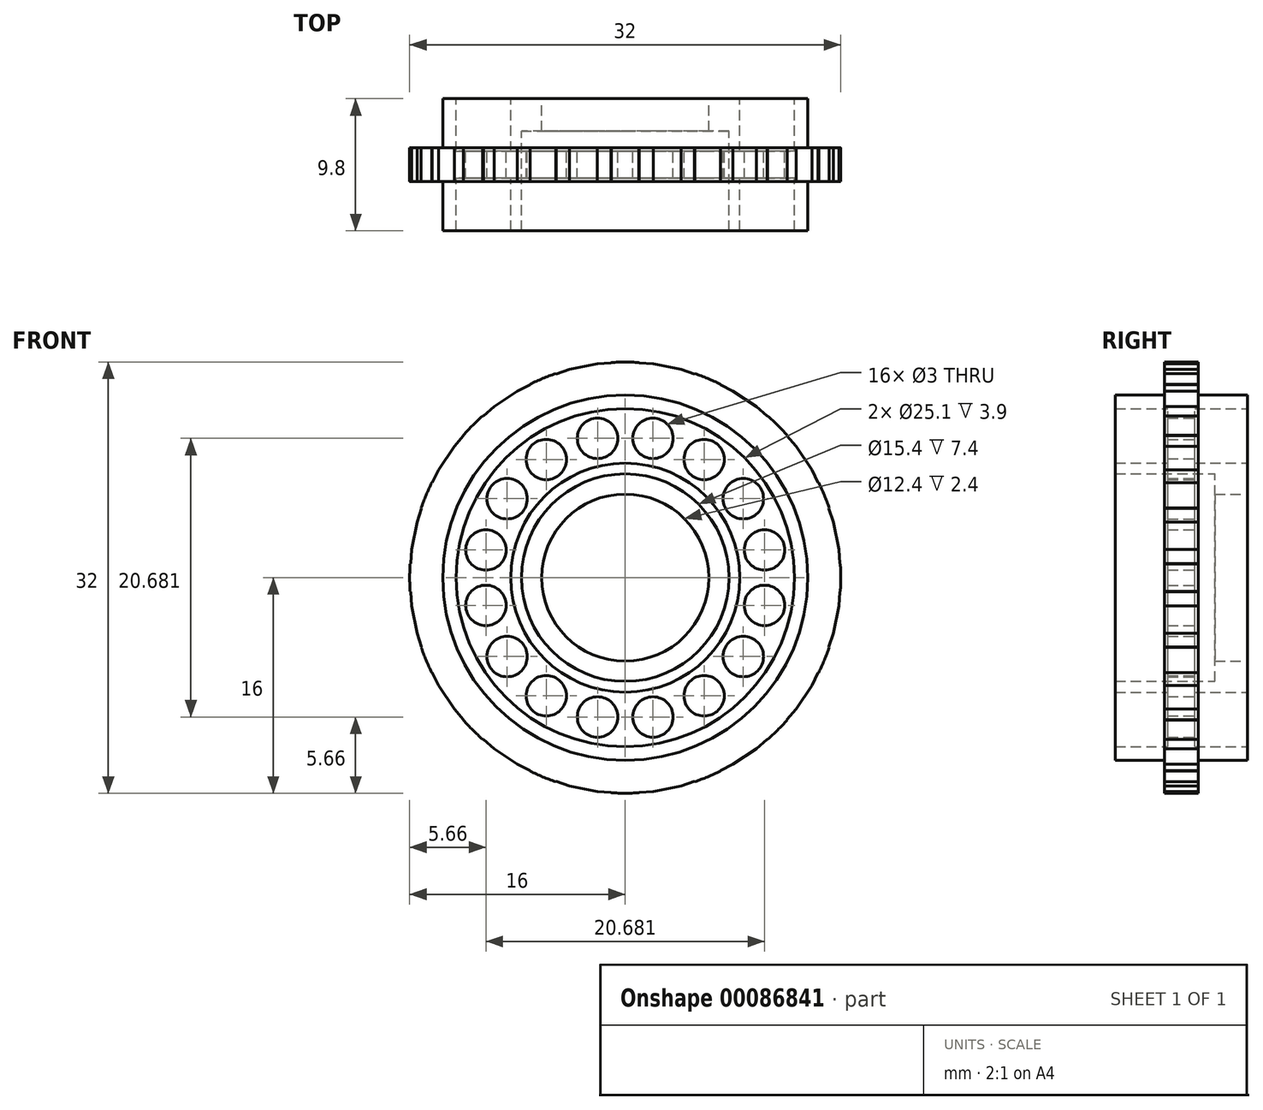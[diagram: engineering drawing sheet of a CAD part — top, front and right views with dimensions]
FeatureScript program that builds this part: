
annotation { "Feature Type Name" : "Feature", "Feature Type Description" : "" }
export const myFeature = defineFeature(function(context is Context, id is Id, definition is map)
    precondition{}
    {
        {
            var Q0;
            Q0=qCreatedBy(makeId("Front.planeOp"),FACE);
            var sketch = newSketch(context, id + "F0", { "sketchPlane" : qUnion([Q0])});
            skCircle(sketch, "E0", {"center": v(0, 0) * mm, "radius": 13.55 * mm});
            skCircle(sketch, "E1", {"center": v(0, 0) * mm, "radius": 12.55 * mm});
            skCircle(sketch, "E2", {"center": v(0, 0) * mm, "radius": 7.7 * mm});
            skCircle(sketch, "E3", {"center": v(0, 0) * mm, "radius": 8.5 * mm});
            skLineSegment(sketch, "E4.1", {"start": v(2.09, 15.86) * mm, "end": v(4.14, 15.45) * mm});
            skLineSegment(sketch, "E4.4", {"start": v(8, 13.86) * mm, "end": v(9.74, 12.7) * mm});
            skLineSegment(sketch, "E4.7", {"start": v(12.7, 9.74) * mm, "end": v(13.86, 8) * mm});
            skLineSegment(sketch, "E4.10", {"start": v(15.45, 4.14) * mm, "end": v(15.86, 2.09) * mm});
            skLineSegment(sketch, "E4.13", {"start": v(15.86, -2.09) * mm, "end": v(15.45, -4.14) * mm});
            skLineSegment(sketch, "E4.16", {"start": v(13.86, -8) * mm, "end": v(12.7, -9.74) * mm});
            skLineSegment(sketch, "E4.19", {"start": v(9.74, -12.7) * mm, "end": v(8, -13.86) * mm});
            skLineSegment(sketch, "E4.22", {"start": v(4.14, -15.45) * mm, "end": v(2.09, -15.86) * mm});
            skLineSegment(sketch, "E4.25", {"start": v(-2.09, -15.86) * mm, "end": v(-4.14, -15.45) * mm});
            skLineSegment(sketch, "E4.28", {"start": v(-8, -13.86) * mm, "end": v(-9.74, -12.7) * mm});
            skLineSegment(sketch, "E4.31", {"start": v(-12.7, -9.74) * mm, "end": v(-13.86, -8) * mm});
            skLineSegment(sketch, "E4.34", {"start": v(-15.45, -4.14) * mm, "end": v(-15.86, -2.09) * mm});
            skLineSegment(sketch, "E4.37", {"start": v(-15.86, 2.09) * mm, "end": v(-15.45, 4.14) * mm});
            skLineSegment(sketch, "E4.40", {"start": v(-13.86, 8) * mm, "end": v(-12.7, 9.74) * mm});
            skLineSegment(sketch, "E4.43", {"start": v(-9.74, 12.7) * mm, "end": v(-8, 13.86) * mm});
            skLineSegment(sketch, "E4.46", {"start": v(-4.14, 15.45) * mm, "end": v(-2.09, 15.86) * mm});
            skLineSegment(sketch, "E5", {"start": v(-1.04, 15.93) * mm, "end": v(0, 17.55) * mm});
            skLineSegment(sketch, "E6", {"start": v(0, 17.55) * mm, "end": v(1.04, 15.93) * mm});
            skLineSegment(sketch, "E7", {"start": v(-6.72, 16.21) * mm, "end": v(-7.06, 14.32) * mm});
            skLineSegment(sketch, "E8", {"start": v(-6.72, 16.21) * mm, "end": v(-5.13, 15.12) * mm});
            skLineSegment(sketch, "E9", {"start": v(6.72, 16.21) * mm, "end": v(5.13, 15.12) * mm});
            skLineSegment(sketch, "E10", {"start": v(6.72, 16.21) * mm, "end": v(7.06, 14.32) * mm});
            skLineSegment(sketch, "E11", {"start": v(10.53, 12) * mm, "end": v(12.4, 12.4) * mm});
            skLineSegment(sketch, "E12", {"start": v(12.4, 12.4) * mm, "end": v(12, 10.53) * mm});
            skLineSegment(sketch, "E13", {"start": v(14.32, 7.06) * mm, "end": v(16.21, 6.72) * mm});
            skLineSegment(sketch, "E14", {"start": v(16.21, 6.72) * mm, "end": v(15.12, 5.13) * mm});
            skLineSegment(sketch, "E15", {"start": v(15.93, 1.04) * mm, "end": v(17.55, 0) * mm});
            skLineSegment(sketch, "E16", {"start": v(17.55, 0) * mm, "end": v(15.93, -1.04) * mm});
            skLineSegment(sketch, "E17", {"start": v(-10.53, 12) * mm, "end": v(-12.4, 12.4) * mm});
            skLineSegment(sketch, "E18", {"start": v(-12, 10.53) * mm, "end": v(-12.4, 12.4) * mm});
            skLineSegment(sketch, "E19", {"start": v(-14.32, 7.06) * mm, "end": v(-16.21, 6.72) * mm});
            skLineSegment(sketch, "E20", {"start": v(-15.12, 5.13) * mm, "end": v(-16.21, 6.72) * mm});
            skLineSegment(sketch, "E21", {"start": v(-15.93, 1.04) * mm, "end": v(-17.55, 0) * mm});
            skLineSegment(sketch, "E22", {"start": v(-15.93, -1.04) * mm, "end": v(-17.55, 0) * mm});
            skLineSegment(sketch, "E23", {"start": v(-15.12, -5.13) * mm, "end": v(-16.21, -6.72) * mm});
            skLineSegment(sketch, "E24", {"start": v(-14.32, -7.06) * mm, "end": v(-16.21, -6.72) * mm});
            skLineSegment(sketch, "E25", {"start": v(-12, -10.53) * mm, "end": v(-12.4, -12.4) * mm});
            skLineSegment(sketch, "E26", {"start": v(-10.53, -12) * mm, "end": v(-12.4, -12.4) * mm});
            skLineSegment(sketch, "E27", {"start": v(-7.06, -14.32) * mm, "end": v(-6.72, -16.21) * mm});
            skLineSegment(sketch, "E28", {"start": v(-5.13, -15.12) * mm, "end": v(-6.72, -16.21) * mm});
            skLineSegment(sketch, "E29", {"start": v(-1.04, -15.93) * mm, "end": v(0, -17.55) * mm});
            skLineSegment(sketch, "E30", {"start": v(1.04, -15.93) * mm, "end": v(0, -17.55) * mm});
            skLineSegment(sketch, "E31", {"start": v(5.13, -15.12) * mm, "end": v(6.72, -16.21) * mm});
            skLineSegment(sketch, "E32", {"start": v(7.06, -14.32) * mm, "end": v(6.72, -16.21) * mm});
            skLineSegment(sketch, "E33", {"start": v(10.53, -12) * mm, "end": v(12.4, -12.4) * mm});
            skLineSegment(sketch, "E34", {"start": v(12, -10.53) * mm, "end": v(12.4, -12.4) * mm});
            skLineSegment(sketch, "E35", {"start": v(14.32, -7.06) * mm, "end": v(16.21, -6.72) * mm});
            skLineSegment(sketch, "E36", {"start": v(15.12, -5.13) * mm, "end": v(16.21, -6.72) * mm});
            skLineSegment(sketch, "E37", {"start": v(0, 12.55) * mm, "end": v(0, 8.5) * mm, "construction": true});
            skCircle(sketch, "E38.cCircle", {"center": v(0, 0) * mm, "radius": 10.34 * mm, "construction": true});
            skLineSegment(sketch, "E38.0", {"start": v(-2.06, 10.34) * mm, "end": v(2.06, 10.34) * mm, "construction": true});
            skLineSegment(sketch, "E38.1", {"start": v(2.06, 10.34) * mm, "end": v(5.86, 8.77) * mm, "construction": true});
            skLineSegment(sketch, "E38.2", {"start": v(5.86, 8.77) * mm, "end": v(8.77, 5.86) * mm, "construction": true});
            skLineSegment(sketch, "E38.3", {"start": v(8.77, 5.86) * mm, "end": v(10.34, 2.06) * mm, "construction": true});
            skLineSegment(sketch, "E38.4", {"start": v(10.34, 2.06) * mm, "end": v(10.34, -2.06) * mm, "construction": true});
            skLineSegment(sketch, "E38.5", {"start": v(10.34, -2.06) * mm, "end": v(8.77, -5.86) * mm, "construction": true});
            skLineSegment(sketch, "E38.6", {"start": v(8.77, -5.86) * mm, "end": v(5.86, -8.77) * mm, "construction": true});
            skLineSegment(sketch, "E38.7", {"start": v(5.86, -8.77) * mm, "end": v(2.06, -10.34) * mm, "construction": true});
            skLineSegment(sketch, "E38.8", {"start": v(2.06, -10.34) * mm, "end": v(-2.06, -10.34) * mm, "construction": true});
            skLineSegment(sketch, "E38.9", {"start": v(-2.06, -10.34) * mm, "end": v(-5.86, -8.77) * mm, "construction": true});
            skLineSegment(sketch, "E38.10", {"start": v(-5.86, -8.77) * mm, "end": v(-8.77, -5.86) * mm, "construction": true});
            skLineSegment(sketch, "E38.11", {"start": v(-8.77, -5.86) * mm, "end": v(-10.34, -2.06) * mm, "construction": true});
            skLineSegment(sketch, "E38.12", {"start": v(-10.34, -2.06) * mm, "end": v(-10.34, 2.06) * mm, "construction": true});
            skLineSegment(sketch, "E38.13", {"start": v(-10.34, 2.06) * mm, "end": v(-8.77, 5.86) * mm, "construction": true});
            skLineSegment(sketch, "E38.14", {"start": v(-8.77, 5.86) * mm, "end": v(-5.86, 8.77) * mm, "construction": true});
            skLineSegment(sketch, "E38.15", {"start": v(-5.86, 8.77) * mm, "end": v(-2.06, 10.34) * mm, "construction": true});
            skCircle(sketch, "E39", {"center": v(-5.86, 8.77) * mm, "radius": 1.5 * mm});
            skCircle(sketch, "E40", {"center": v(-2.06, 10.34) * mm, "radius": 1.5 * mm});
            skCircle(sketch, "E41", {"center": v(2.06, 10.34) * mm, "radius": 1.5 * mm});
            skCircle(sketch, "E42", {"center": v(5.86, 8.77) * mm, "radius": 1.5 * mm});
            skCircle(sketch, "E43", {"center": v(8.77, 5.86) * mm, "radius": 1.5 * mm});
            skCircle(sketch, "E44", {"center": v(10.34, 2.06) * mm, "radius": 1.5 * mm});
            skCircle(sketch, "E45", {"center": v(10.34, -2.06) * mm, "radius": 1.5 * mm});
            skCircle(sketch, "E46", {"center": v(8.77, -5.86) * mm, "radius": 1.5 * mm});
            skCircle(sketch, "E47", {"center": v(5.86, -8.77) * mm, "radius": 1.5 * mm});
            skCircle(sketch, "E48", {"center": v(2.06, -10.34) * mm, "radius": 1.5 * mm});
            skCircle(sketch, "E49", {"center": v(-2.06, -10.34) * mm, "radius": 1.5 * mm});
            skCircle(sketch, "E50", {"center": v(-5.86, -8.77) * mm, "radius": 1.5 * mm});
            skCircle(sketch, "E51", {"center": v(-8.77, -5.86) * mm, "radius": 1.5 * mm});
            skCircle(sketch, "E52", {"center": v(-10.34, -2.06) * mm, "radius": 1.5 * mm});
            skCircle(sketch, "E53", {"center": v(-10.34, 2.06) * mm, "radius": 1.5 * mm});
            skCircle(sketch, "E54", {"center": v(-8.77, 5.86) * mm, "radius": 1.5 * mm});
            skLineSegment(sketch, "E55", {"start": v(-15.45, 4.14) * mm, "end": v(-15.12, 5.13) * mm});
            skLineSegment(sketch, "E56", {"start": v(-14.32, 7.06) * mm, "end": v(-13.86, 8) * mm});
            skLineSegment(sketch, "E57", {"start": v(-12.7, 9.74) * mm, "end": v(-12, 10.53) * mm});
            skLineSegment(sketch, "E58", {"start": v(-10.53, 12) * mm, "end": v(-9.74, 12.7) * mm});
            skLineSegment(sketch, "E59", {"start": v(-8, 13.86) * mm, "end": v(-7.06, 14.32) * mm});
            skLineSegment(sketch, "E60", {"start": v(-5.13, 15.12) * mm, "end": v(-4.14, 15.45) * mm});
            skLineSegment(sketch, "E61", {"start": v(-2.09, 15.86) * mm, "end": v(-1.04, 15.93) * mm});
            skLineSegment(sketch, "E62", {"start": v(1.04, 15.93) * mm, "end": v(2.09, 15.86) * mm});
            skLineSegment(sketch, "E63", {"start": v(4.14, 15.45) * mm, "end": v(5.13, 15.12) * mm});
            skLineSegment(sketch, "E64", {"start": v(7.06, 14.32) * mm, "end": v(8, 13.86) * mm});
            skLineSegment(sketch, "E65", {"start": v(9.74, 12.7) * mm, "end": v(10.53, 12) * mm});
            skLineSegment(sketch, "E66", {"start": v(12, 10.53) * mm, "end": v(12.7, 9.74) * mm});
            skLineSegment(sketch, "E67", {"start": v(13.86, 8) * mm, "end": v(14.32, 7.06) * mm});
            skLineSegment(sketch, "E68", {"start": v(15.12, 5.13) * mm, "end": v(15.45, 4.14) * mm});
            skLineSegment(sketch, "E69", {"start": v(15.86, 2.09) * mm, "end": v(15.93, 1.04) * mm});
            skLineSegment(sketch, "E70", {"start": v(15.93, -1.04) * mm, "end": v(15.86, -2.09) * mm});
            skLineSegment(sketch, "E71", {"start": v(15.45, -4.14) * mm, "end": v(15.12, -5.13) * mm});
            skLineSegment(sketch, "E72", {"start": v(14.32, -7.06) * mm, "end": v(13.86, -8) * mm});
            skLineSegment(sketch, "E73", {"start": v(12.7, -9.74) * mm, "end": v(12, -10.53) * mm});
            skLineSegment(sketch, "E74", {"start": v(10.53, -12) * mm, "end": v(9.74, -12.7) * mm});
            skLineSegment(sketch, "E75", {"start": v(8, -13.86) * mm, "end": v(7.06, -14.32) * mm});
            skLineSegment(sketch, "E76", {"start": v(5.13, -15.12) * mm, "end": v(4.14, -15.45) * mm});
            skLineSegment(sketch, "E77", {"start": v(2.09, -15.86) * mm, "end": v(1.04, -15.93) * mm});
            skLineSegment(sketch, "E78", {"start": v(-1.04, -15.93) * mm, "end": v(-2.09, -15.86) * mm});
            skLineSegment(sketch, "E79", {"start": v(-4.14, -15.45) * mm, "end": v(-5.13, -15.12) * mm});
            skLineSegment(sketch, "E80", {"start": v(-7.06, -14.32) * mm, "end": v(-8, -13.86) * mm});
            skLineSegment(sketch, "E81", {"start": v(-9.74, -12.7) * mm, "end": v(-10.53, -12) * mm});
            skLineSegment(sketch, "E82", {"start": v(-12, -10.53) * mm, "end": v(-12.7, -9.74) * mm});
            skLineSegment(sketch, "E83", {"start": v(-13.86, -8) * mm, "end": v(-14.32, -7.06) * mm});
            skLineSegment(sketch, "E84", {"start": v(-15.12, -5.13) * mm, "end": v(-15.45, -4.14) * mm});
            skLineSegment(sketch, "E85", {"start": v(-15.86, -2.09) * mm, "end": v(-15.93, -1.04) * mm});
            skLineSegment(sketch, "E86", {"start": v(-15.93, 1.04) * mm, "end": v(-15.86, 2.09) * mm});
            skCircle(sketch, "E87", {"center": v(0, 0) * mm, "radius": 16 * mm});
            skSolve(sketch);
        }
        {
            var Q0;
            Q0=makeQuery(id+"F0.imprint","IMPRINT",FACE,{"disambiguationData":[TD([[makeQuery(id+"F0.imprint","IMPRINT",EDGE,{"derivedFrom":sQuery(id+"F0.wireOp",EDGE,"E0")}),-1.0]])]});
            extrude(context, id + "F1", {"entities" : qUnion([Q0]), "depth" : 2.5 * mm, "symmetric" : true});
        }
        {
            var Q0;
            Q0=makeQuery(id+"F0.imprint","IMPRINT",FACE,{"disambiguationData":[TD([[makeQuery(id+"F0.imprint","IMPRINT",EDGE,{"derivedFrom":sQuery(id+"F0.wireOp",EDGE,"E0")}),1.0]])]});
            extrude(context, id + "F2", {"entities" : qUnion([Q0]), "operationType" : NewBodyOperationType.ADD, "depth" : 9.8 * mm, "symmetric" : true});
        }
        {
            var Q0;
            Q0=makeQuery(id+"F0.imprint","IMPRINT",FACE,{"disambiguationData":[TD([[makeQuery(id+"F0.imprint","IMPRINT",EDGE,{"derivedFrom":sQuery(id+"F0.wireOp",EDGE,"E1")}),1.0]])]});
            extrude(context, id + "F3", {"entities" : qUnion([Q0]), "operationType" : NewBodyOperationType.ADD, "depth" : 2 * mm, "symmetric" : true});
        }
        {
            var Q0;
            Q0=makeQuery(id+"F0.imprint","IMPRINT",FACE,{"disambiguationData":[TD([[makeQuery(id+"F0.imprint","IMPRINT",EDGE,{"derivedFrom":sQuery(id+"F0.wireOp",EDGE,"E2")}),-1.0]])]});
            extrude(context, id + "F4", {"entities" : qUnion([Q0]), "operationType" : NewBodyOperationType.ADD, "depth" : 9.8 * mm, "symmetric" : true});
        }
        {
            var Q0;
            Q0=makeQuery(id+"F4.opExtrude","CAP_FACE",FACE,{"disambiguationData":[OSD([sQuery(id+"F0.wireOp",EDGE,"E2"),sQuery(id+"F0.wireOp",EDGE,"E3")])],"isStart":true});
            var sketch = newSketch(context, id + "F5", { "sketchPlane" : qUnion([Q0])});
            skCircle(sketch, "E88", {"center": v(0, 0) * mm, "radius": 6.2 * mm});
            skSolve(sketch);
        }
        {
            var Q0;
            Q0=makeQuery(id+"F5.imprint","IMPRINT",FACE,{"disambiguationData":[TD([[makeQuery(id+"F5.imprint","IMPRINT",EDGE,{"derivedFrom":sQuery(id+"F5.wireOp",EDGE,"E88")}),-1.0]])]});
            extrude(context, id + "F6", {"entities" : qUnion([Q0]), "operationType" : NewBodyOperationType.ADD, "oppositeDirection" : true, "depth" : 2.4 * mm});
        }
    });
